# Revit family: НЕВАТОМ_Шибер-AxB_20220407
name_source: partatom
category: Арматура воздуховодов
revit_build: Autodesk Revit 2017 (Build: 20170118_1100(x64)
units: mm (PartAtom-declared; Revit-internal decimal feet)

## family parameters
Всегда вертикально = Нет
На основе рабочей плоскости = Нет
Общий = Нет
При загрузке вырезать с полостями = Нет
Размер круглого соединителя = Использовать диаметр
Тип детали = Вставляется

## types (12) — shared parameters
190 = 190 мм
20 = 20 мм
ADSK_Единица измерения = шт.
ADSK_Завод-изготовитель = NEVATOM
ADSK_Масса_Текст = кг
ADSK_Материал наименование = Оцинкованная сталь
ADSK_Наименование = Шибер
ADSK_Напряжение = 0 В
ADSK_Полная мощность = 0 В·А
ADSK_Размер_Ширина = 190 мм
ADSK_Ток = 0 А
Nevatom_URL = https://t.me
t = 1 мм
Материал корпуса = Материал корпуса
zero-valued in all types: ADSK_Масса

## per-type parameters (varying)
| type | A | A/2 | A1 | ADSK_Марка | ADSK_Размер_Высота | ADSK_Размер_Длина | B1 | L |
| 100x100 | 100 мм | 70 мм | 165 мм | 100x100–ОЦ.–0,7–T2.T2 | 165 мм | 285 мм | 285 мм | 10 мм |
| 125x125 | 125 мм | 83 мм | 190 мм | 125x125–ОЦ.–0,7–T2.T2 | 190 мм | 335 мм | 335 мм | 15 мм |
| 150x150 | 150 мм | 95 мм | 225 мм | 150x150–ОЦ.–0,7–T2.T2 | 225 мм | 405 мм | 405 мм | 15 мм |
| 200x200 | 200 мм | 120 мм | 265 мм | 200x200–ОЦ.–0,7–T2.T2 | 265 мм | 485 мм | 485 мм | 15 мм |
| 250x250 | 250 мм | 145 мм | 315 мм | 250x250–ОЦ.–0,7–T2.T2 | 315 мм | 585 мм | 585 мм | 15 мм |
| 300x300 | 300 мм | 170 мм | 375 мм | 300x300–ОЦ.–0,7–T2.T2 | 375 мм | 695 мм | 695 мм | 15 мм |
| 350x350 | 350 мм | 195 мм | 415 мм | 350x350–ОЦ.–0,7–T2.T2 | 415 мм | 785 мм | 785 мм | 15 мм |
| 400x400 | 400 мм | 220 мм | 460 мм | 400x400–ОЦ.–0,7–T2.T2 | 460 мм | 885 мм | 885 мм | 15 мм |
| 450x450 | 450 мм | 245 мм | 515 мм | 450x450–ОЦ.–0,7–T2.T2 | 515 мм | 985 мм | 985 мм | 15 мм |
| 500x500 | 500 мм | 270 мм | 565 мм | 500x500–ОЦ.–0,7–T2.T2 | 565 мм | 1085 мм | 1085 мм | 15 мм |
| 560x560 | 560 мм | 300 мм | 625 мм | 560x560–ОЦ.–0,7–T2.T2 | 625 мм | 1145 мм | 1145 мм | 15 мм |
| 600x600 | 600 мм | 320 мм | 665 мм | 600x600–ОЦ.–0,7–T2.T2 | 665 мм | 1285 мм | 1285 мм | 15 мм |
